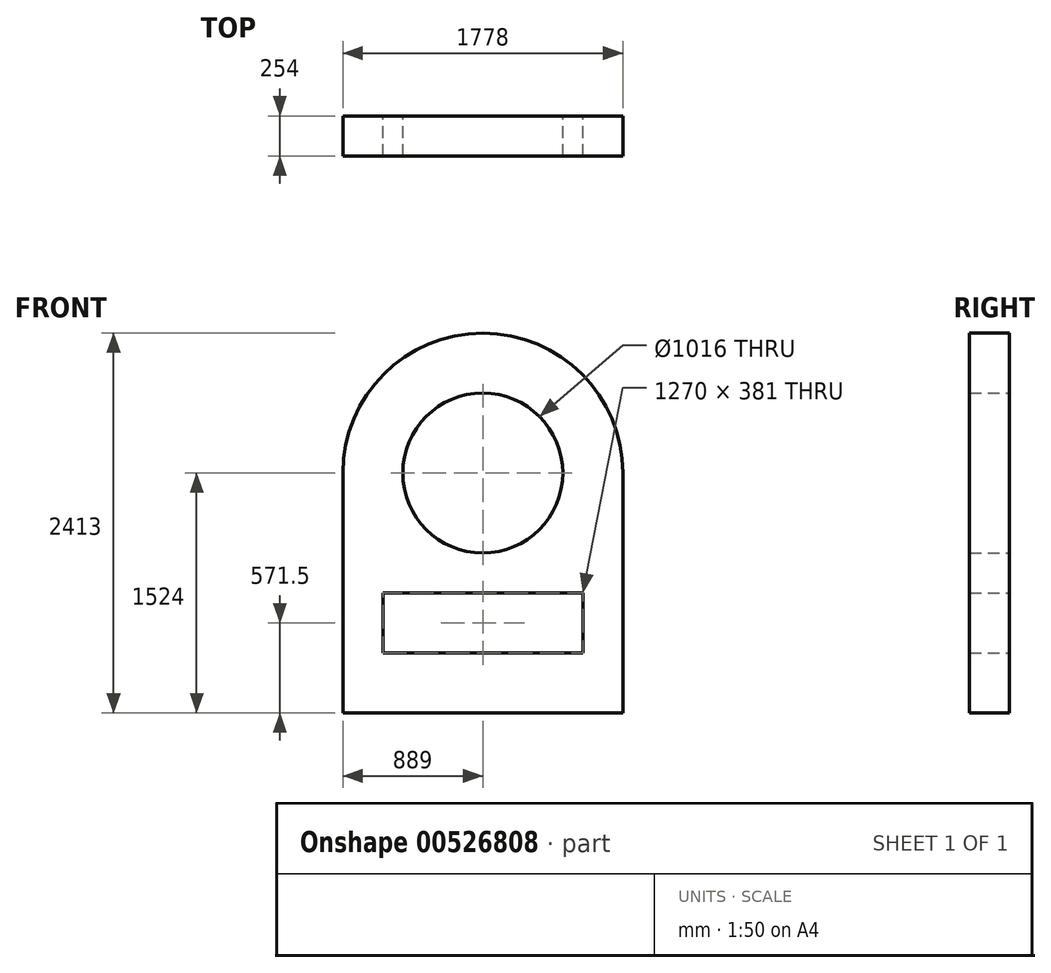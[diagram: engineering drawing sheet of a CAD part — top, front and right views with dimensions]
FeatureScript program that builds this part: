
annotation { "Feature Type Name" : "Feature", "Feature Type Description" : "" }
export const myFeature = defineFeature(function(context is Context, id is Id, definition is map)
    precondition{}
    {
        {
            var Q0;
            Q0=qCreatedBy(makeId("Front.planeOp"),FACE);
            var sketch = newSketch(context, id + "F0", { "sketchPlane" : qUnion([Q0])});
            skLineSegment(sketch, "E0", {"start": v(0, 0) * mm, "end": v(1778, 0) * mm});
            skLineSegment(sketch, "E1", {"start": v(1778, 0) * mm, "end": v(1778, 1524) * mm});
            skLineSegment(sketch, "E2", {"start": v(0, 0) * mm, "end": v(0, 1524) * mm});
            skArc(sketch, "E3", {"start": v(1778, 1524) * mm, "mid": v(889, 2413) * mm, "end": v(0, 1524) * mm});
            skCircle(sketch, "E4", {"center": v(889, 1524) * mm, "radius": 508 * mm});
            skLineSegment(sketch, "E5", {"start": v(254, 762) * mm, "end": v(1524, 762) * mm});
            skLineSegment(sketch, "E6", {"start": v(1524, 762) * mm, "end": v(1524, 381) * mm});
            skLineSegment(sketch, "E7", {"start": v(1524, 381) * mm, "end": v(254, 381) * mm});
            skLineSegment(sketch, "E8", {"start": v(254, 381) * mm, "end": v(254, 762) * mm});
            skSolve(sketch);
        }
        {
            var Q0;
            Q0 = qSketchRegion(id + "F0", true);
            extrude(context, id + "F1", {"entities" : qUnion([Q0]), "depth" : 254 * mm, "offsetDistance" : 25.4 * mm});
        }
    });
